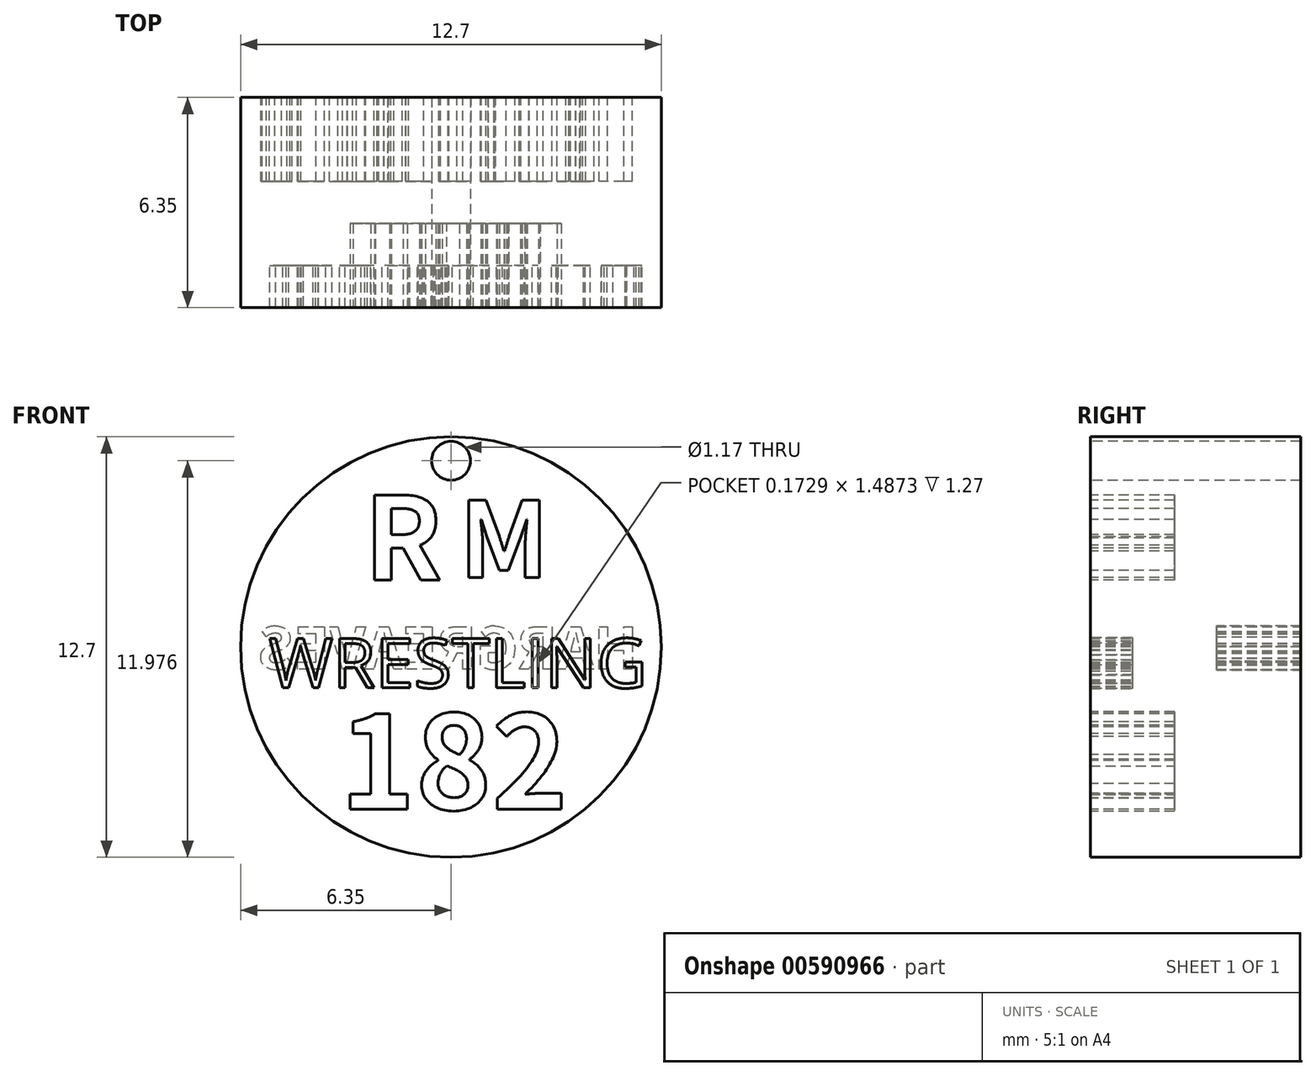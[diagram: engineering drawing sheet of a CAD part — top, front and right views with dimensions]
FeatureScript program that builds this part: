
annotation { "Feature Type Name" : "Feature", "Feature Type Description" : "" }
export const myFeature = defineFeature(function(context is Context, id is Id, definition is map)
    precondition{}
    {
        {
            var Q0;
            Q0=qCreatedBy(makeId("Front.planeOp"),FACE);
            var sketch = newSketch(context, id + "F0", { "sketchPlane" : qUnion([Q0])});
            skCircle(sketch, "E0", {"center": v(0, 0) * mm, "radius": 6.35 * mm});
            skSolve(sketch);
        }
        {
            var Q0;
            Q0=makeQuery(id+"F0.imprint","IMPRINT",FACE,{"disambiguationData":[TD([[makeQuery(id+"F0.imprint","IMPRINT",EDGE,{"derivedFrom":sQuery(id+"F0.wireOp",EDGE,"E0")}),1.0]])]});
            extrude(context, id + "F1", {"entities" : qUnion([Q0]), "depth" : 6.35 * mm, "offsetDistance" : 25.4 * mm});
        }
        {
            var Q0;
            Q0=makeQuery(id+"F1.opExtrude","CAP_FACE",FACE,{"disambiguationData":[OSD([sQuery(id+"F0.wireOp",EDGE,"E0")])],"isStart":false});
            var sketch = newSketch(context, id + "F2", { "sketchPlane" : qUnion([Q0])});
            skText(sketch, "E1", { "text": "RM", "fontName": "NotoSansCJKjp-Bold.otf"});
            const initialGuessF2  = {"E1": [-0.00263, 0.00202, 1, 0, 0.0025]};
            skSetInitialGuess(sketch, initialGuessF2);
            skSolve(sketch);
        }
        {
            var Q0;
            Q0=makeQuery(id+"F2.imprint","IMPRINT",FACE,{"disambiguationData":[TD([[makeQuery(id+"F2.imprint","IMPRINT",EDGE,{"derivedFrom":sQuery(id+"F2.wireOp",EDGE,"E1.sketch_text.stroke-0")}),1.0]])]});
            extrude(context, id + "F3", {"entities" : qUnion([Q0]), "operationType" : NewBodyOperationType.REMOVE, "oppositeDirection" : true, "depth" : 2.54 * mm, "offsetDistance" : 25.4 * mm});
        }
        {
            var Q0;
            {var subQ0=sQuery(id+"F0.wireOp",EDGE,"E0");Q0=makeQuery(id+"F3.boolean.opBoolean","SPLIT",FACE,{"disambiguationData":[TD([makeQuery(id+"F1.opExtrude","SWEPT_FACE",FACE,{"disambiguationData":[OSD([subQ0])]})])],"derivedFrom":makeQuery(id+"F1.opExtrude","CAP_FACE",FACE,{"disambiguationData":[OSD([subQ0])],"isStart":false})});}
            var sketch = newSketch(context, id + "F4", { "sketchPlane" : qUnion([Q0])});
            skText(sketch, "E2", { "text": "M", "fontName": "NotoSansCJKjp-Bold.otf"});
            const initialGuessF4  = {"E2": [0.00025, 0.0021, 1, 0, 0.00228]};
            skSetInitialGuess(sketch, initialGuessF4);
            skSolve(sketch);
        }
        {
            var Q0;
            Q0=makeQuery(id+"F4.imprint","IMPRINT",FACE,{"disambiguationData":[TD([[makeQuery(id+"F4.imprint","IMPRINT",EDGE,{"derivedFrom":sQuery(id+"F4.wireOp",EDGE,"E2.sketch_text.stroke-0")}),1.0]])]});
            extrude(context, id + "F5", {"entities" : qUnion([Q0]), "operationType" : NewBodyOperationType.REMOVE, "oppositeDirection" : true, "depth" : 2.54 * mm, "offsetDistance" : 25.4 * mm});
        }
        {
            var Q0;
            {var subQ0=sQuery(id+"F0.wireOp",EDGE,"E0");Q0=makeQuery(id+"F3.boolean.opBoolean","SPLIT",FACE,{"disambiguationData":[TD([makeQuery(id+"F1.opExtrude","SWEPT_FACE",FACE,{"disambiguationData":[OSD([subQ0])]})])],"derivedFrom":makeQuery(id+"F1.opExtrude","CAP_FACE",FACE,{"disambiguationData":[OSD([subQ0])],"isStart":false})});}
            var sketch = newSketch(context, id + "F6", { "sketchPlane" : qUnion([Q0])});
            skText(sketch, "E3", { "text": "WRESTLING", "fontName": "OpenSans-Regular.ttf"});
            const initialGuessF6  = {"E3": [-0.0055, -0.00123, 1, 0, 0.0015]};
            skSetInitialGuess(sketch, initialGuessF6);
            skSolve(sketch);
        }
        {
            var Q0;
            Q0 = qSketchRegion(id + "F6", true);
            extrude(context, id + "F7", {"entities" : qUnion([Q0]), "operationType" : NewBodyOperationType.REMOVE, "endBound" : BoundingType.SYMMETRIC, "depth" : 2.54 * mm, "offsetDistance" : 25.4 * mm});
        }
        {
            var Q0;
            {var subQ10=sQuery(id+"F0.wireOp",EDGE,"E0");var subQ11=makeQuery(id+"F1.opExtrude","SWEPT_FACE",FACE,{"disambiguationData":[OSD([subQ10])]});Q0=makeQuery(id+"F7.boolean.opBoolean","SPLIT",FACE,{"disambiguationData":[TD([subQ11])],"derivedFrom":makeQuery(id+"F3.boolean.opBoolean","SPLIT",FACE,{"disambiguationData":[TD([subQ11])],"derivedFrom":makeQuery(id+"F1.opExtrude","CAP_FACE",FACE,{"disambiguationData":[OSD([subQ10])],"isStart":false})})});}
            var sketch = newSketch(context, id + "F8", { "sketchPlane" : qUnion([Q0])});
            skText(sketch, "E4", { "text": "182", "fontName": "NotoSansCJKjp-Bold.otf"});
            const initialGuessF8  = {"E4": [-0.00337, -0.0049, 1, 0, 0.00281]};
            skSetInitialGuess(sketch, initialGuessF8);
            skSolve(sketch);
        }
        {
            var Q0;
            Q0 = qSketchRegion(id + "F8", true);
            extrude(context, id + "F9", {"entities" : qUnion([Q0]), "operationType" : NewBodyOperationType.REMOVE, "oppositeDirection" : true, "depth" : 2.54 * mm, "offsetDistance" : 25.4 * mm});
        }
        {
            var Q0;
            Q0=makeQuery(id+"F1.opExtrude","CAP_FACE",FACE,{"disambiguationData":[OSD([sQuery(id+"F0.wireOp",EDGE,"E0")])],"isStart":true});
            var sketch = newSketch(context, id + "F10", { "sketchPlane" : qUnion([Q0])});
            skText(sketch, "E5", { "text": "HARGREAVES", "fontName": "NotoSansCJKjp-Bold.otf"});
            const initialGuessF10  = {"E5": [-0.00563, -0.00067, 1, 0, 0.00125]};
            skSetInitialGuess(sketch, initialGuessF10);
            skSolve(sketch);
        }
        {
            var Q0;
            Q0 = qSketchRegion(id + "F10", true);
            extrude(context, id + "F11", {"entities" : qUnion([Q0]), "operationType" : NewBodyOperationType.REMOVE, "oppositeDirection" : true, "depth" : 2.54 * mm, "offsetDistance" : 25.4 * mm});
        }
        {
            var Q0;
            {var subQ90=sQuery(id+"F0.wireOp",EDGE,"E0");var subQ91=makeQuery(id+"F1.opExtrude","SWEPT_FACE",FACE,{"disambiguationData":[OSD([subQ90])]});Q0=makeQuery(id+"F9.boolean.opBoolean","SPLIT",FACE,{"disambiguationData":[TD([subQ91])],"derivedFrom":makeQuery(id+"F7.boolean.opBoolean","SPLIT",FACE,{"disambiguationData":[TD([subQ91])],"derivedFrom":makeQuery(id+"F3.boolean.opBoolean","SPLIT",FACE,{"disambiguationData":[TD([subQ91])],"derivedFrom":makeQuery(id+"F1.opExtrude","CAP_FACE",FACE,{"disambiguationData":[OSD([subQ90])],"isStart":false})})})});}
            var sketch = newSketch(context, id + "F12", { "sketchPlane" : qUnion([Q0])});
            skCircle(sketch, "E6", {"center": v(0, 5.63) * mm, "radius": 0.59 * mm});
            skSolve(sketch);
        }
        {
            var Q0;
            Q0=makeQuery(id+"F12.imprint","IMPRINT",FACE,{"disambiguationData":[TD([[makeQuery(id+"F12.imprint","IMPRINT",EDGE,{"derivedFrom":sQuery(id+"F12.wireOp",EDGE,"E6")}),1.0]])]});
            extrude(context, id + "F13", {"entities" : qUnion([Q0]), "operationType" : NewBodyOperationType.REMOVE, "oppositeDirection" : true, "depth" : 12.7 * mm, "offsetDistance" : 25.4 * mm});
        }
    });
